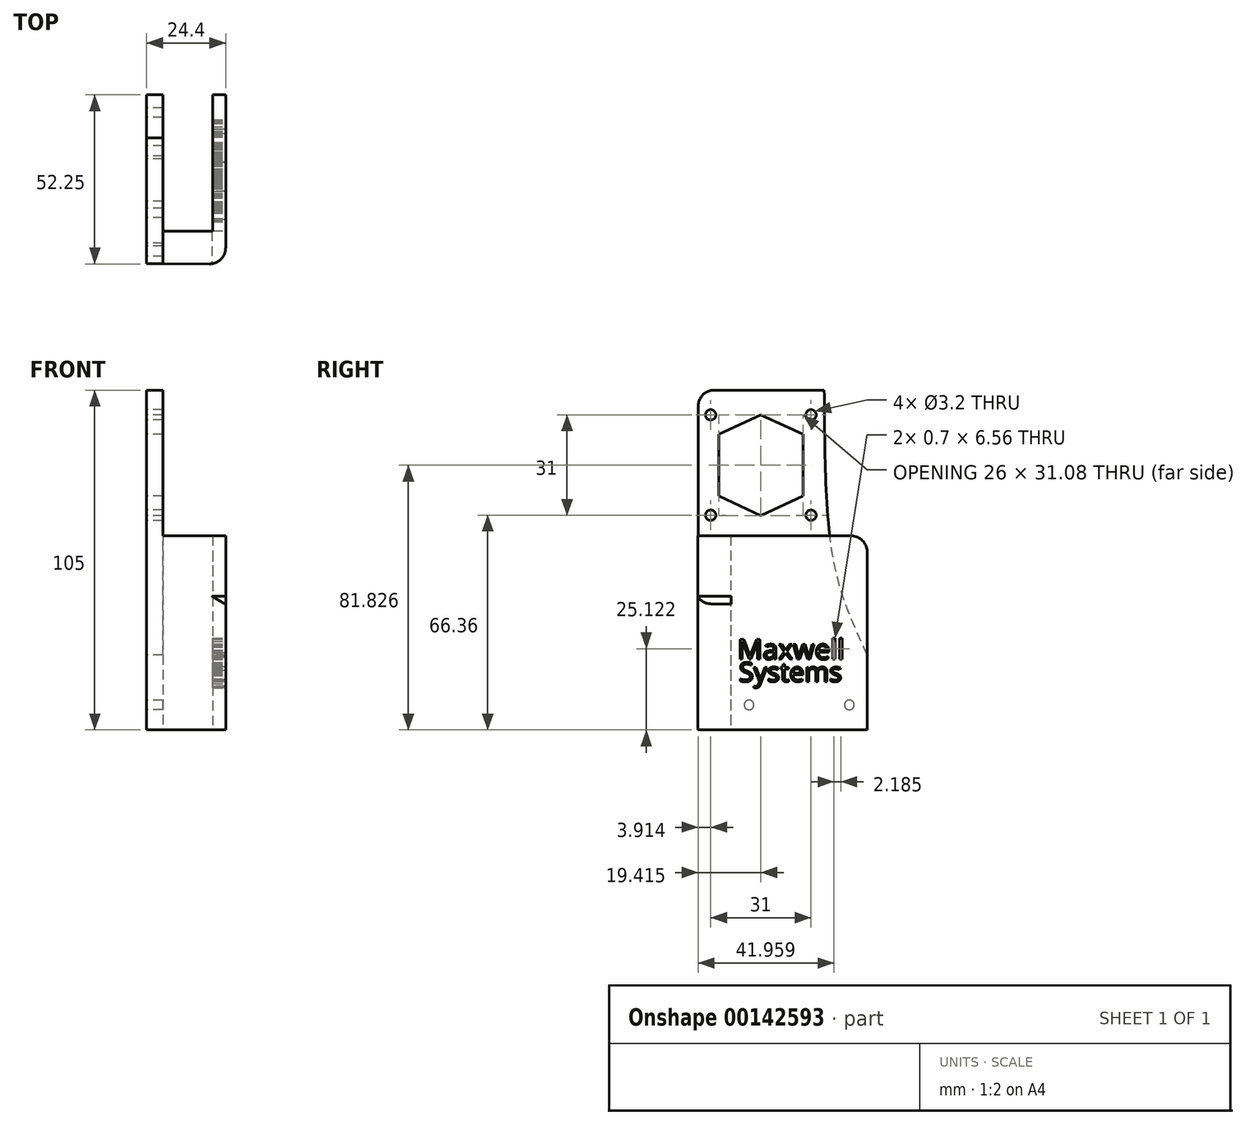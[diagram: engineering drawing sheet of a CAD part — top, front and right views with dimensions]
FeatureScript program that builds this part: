
annotation { "Feature Type Name" : "Feature", "Feature Type Description" : "" }
export const myFeature = defineFeature(function(context is Context, id is Id, definition is map)
    precondition{}
    {
        {
            var Q0;
            Q0=qCreatedBy(makeId("Top.planeOp"),FACE);
            var sketch = newSketch(context, id + "F0", { "sketchPlane" : qUnion([Q0])});
            skLineSegment(sketch, "E0.bottom", {"start": v(0, 0) * mm, "end": v(-15, 0) * mm});
            skLineSegment(sketch, "E0.top", {"start": v(0, 42) * mm, "end": v(-15, 42) * mm});
            skLineSegment(sketch, "E0.left", {"start": v(0, 0) * mm, "end": v(0, 42) * mm});
            skLineSegment(sketch, "E0.right", {"start": v(-15, 0) * mm, "end": v(-15, 42) * mm});
            skLineSegment(sketch, "E1.0", {"start": v(-15.2, -0.02) * mm, "end": v(-15.2, 42) * mm});
            skLineSegment(sketch, "E2.bottom", {"start": v(-15.2, 42) * mm, "end": v(-20.2, 42) * mm});
            skLineSegment(sketch, "E2.left", {"start": v(-15.2, 42) * mm, "end": v(-15.2, 0) * mm});
            skLineSegment(sketch, "E2.right", {"start": v(-20.2, 42) * mm, "end": v(-20.2, 0) * mm});
            skPoint(sketch, "E3.right.end.orphan", {"position": v(-20.2, -5.2) * mm});
            skLineSegment(sketch, "E4", {"start": v(-20.2, 0) * mm, "end": v(-20.2, -10.2) * mm});
            skLineSegment(sketch, "E5", {"start": v(-15.2, -0.02) * mm, "end": v(-15.2, -0.2) * mm});
            skLineSegment(sketch, "E6", {"start": v(-20.2, -10.2) * mm, "end": v(-15.2, -10.22) * mm});
            skLineSegment(sketch, "E7.0", {"start": v(0, -0.2) * mm, "end": v(-15, -0.2) * mm});
            skLineSegment(sketch, "E8", {"start": v(-15, -0.2) * mm, "end": v(-15.2, -0.2) * mm});
            skLineSegment(sketch, "E9.0", {"start": v(0.2, 0) * mm, "end": v(0.2, 41.89) * mm});
            skLineSegment(sketch, "E10", {"start": v(0.2, -0.2) * mm, "end": v(0, -0.2) * mm});
            skLineSegment(sketch, "E11", {"start": v(0.2, -0.2) * mm, "end": v(0.2, 0) * mm});
            skLineSegment(sketch, "E12.left", {"start": v(0.2, 41.89) * mm, "end": v(0.2, -0.2) * mm});
            skLineSegment(sketch, "E12.right", {"start": v(4.2, 41.89) * mm, "end": v(4.2, -10.27) * mm});
            skLineSegment(sketch, "E13", {"start": v(0, 42) * mm, "end": v(4.2, 42) * mm});
            skLineSegment(sketch, "E14", {"start": v(4.2, 41.89) * mm, "end": v(4.2, 42) * mm});
            skLineSegment(sketch, "E15", {"start": v(0.2, 41.89) * mm, "end": v(0.2, 42) * mm});
            skLineSegment(sketch, "E16", {"start": v(-15.2, -0.2) * mm, "end": v(-15.2, -10.22) * mm});
            skLineSegment(sketch, "E17", {"start": v(-15.2, -10.22) * mm, "end": v(4.2, -10.27) * mm});
            skSolve(sketch);
        }
        {
            var Q0;
            Q0=makeQuery(id+"F0.imprint","IMPRINT",FACE,{"disambiguationData":[TD([[makeQuery(id+"F0.imprint","IMPRINT",EDGE,{"derivedFrom":sQuery(id+"F0.wireOp",EDGE,"E2.bottom")}),1.0]])]});
            extrude(context, id + "F1", {"entities" : qUnion([Q0]), "depth" : 105 * mm});
        }
        {
            var Q0;
            Q0=makeQuery(id+"F1.opExtrude","SWEPT_FACE",FACE,{"disambiguationData":[OSD([sQuery(id+"F0.wireOp",EDGE,"E2.right"),sQuery(id+"F0.wireOp",EDGE,"E3.right"),sQuery(id+"F0.wireOp",EDGE,"qdzb2MuQ-bYxo-XKaB-Kbji-J9fmD8T30UYQ")])]});
            var sketch = newSketch(context, id + "F2", { "sketchPlane" : qUnion([Q0])});
            skCircle(sketch, "E18", {"center": v(-36.5, 7.75) * mm, "radius": 1.5 * mm});
            skCircle(sketch, "E19", {"center": v(-5.5, 7.75) * mm, "radius": 1.5 * mm});
            skLineSegment(sketch, "E20", {"start": v(-36.5, 7.75) * mm, "end": v(-42, 7.75) * mm, "construction": true});
            skLineSegment(sketch, "E21", {"start": v(-42, 7.75) * mm, "end": v(-42, 0) * mm, "construction": true});
            skLineSegment(sketch, "E22", {"start": v(-36.5, 7.75) * mm, "end": v(-5.5, 7.75) * mm, "construction": true});
            skSolve(sketch);
        }
        {
            var Q0;
            Q0=makeQuery(id+"F2.imprint","IMPRINT",FACE,{"disambiguationData":[TD([[makeQuery(id+"F2.imprint","IMPRINT",EDGE,{"derivedFrom":sQuery(id+"F2.wireOp",EDGE,"E18")}),1.0]])]});
            var Q1;
            Q1=makeQuery(id+"F2.imprint","IMPRINT",FACE,{"disambiguationData":[TD([[makeQuery(id+"F2.imprint","IMPRINT",EDGE,{"derivedFrom":sQuery(id+"F2.wireOp",EDGE,"E19")}),1.0]])]});
            extrude(context, id + "F3", {"entities" : qUnion([Q0, Q1]), "operationType" : NewBodyOperationType.REMOVE, "oppositeDirection" : true, "depth" : 26 * mm});
        }
        {
            var Q0;
            Q0=makeQuery(id+"F1.opExtrude","SWEPT_FACE",FACE,{"disambiguationData":[OSD([sQuery(id+"F0.wireOp",EDGE,"E2.right"),sQuery(id+"F0.wireOp",EDGE,"E3.right"),sQuery(id+"F0.wireOp",EDGE,"qdzb2MuQ-bYxo-XKaB-Kbji-J9fmD8T30UYQ")])]});
            var sketch = newSketch(context, id + "F4", { "sketchPlane" : qUnion([Q0])});
            skLineSegment(sketch, "E23", {"start": v(0, 0) * mm, "end": v(0, 35) * mm, "construction": true});
            skLineSegment(sketch, "E24", {"start": v(0, 35) * mm, "end": v(-9.15, 35) * mm, "construction": true});
            skLineSegment(sketch, "E25", {"start": v(-9.15, 35) * mm, "end": v(-9.15, 81.85) * mm, "construction": true});
            skCircle(sketch, "E26", {"center": v(-24.66, 66.36) * mm, "radius": 1.6 * mm});
            skCircle(sketch, "E27", {"center": v(6.34, 66.36) * mm, "radius": 1.6 * mm});
            skCircle(sketch, "E28", {"center": v(-24.66, 97.36) * mm, "radius": 1.6 * mm});
            skCircle(sketch, "E29", {"center": v(6.34, 97.36) * mm, "radius": 1.6 * mm});
            skPoint(sketch, "E30.endSnap0", {"position": v(-22.16, 81.86) * mm});
            skLineSegment(sketch, "E31.left", {"start": v(-22.16, 74.87) * mm, "end": v(-22.16, 72.36) * mm});
            skLineSegment(sketch, "E31.right", {"start": v(3.84, 74.87) * mm, "end": v(3.84, 72.36) * mm});
            skPoint(sketch, "E31.middle", {"position": v(-9.16, 81.86) * mm});
            skPoint(sketch, "E32.visualSharp", {"position": v(-22.16, 91.36) * mm});
            skPoint(sketch, "E33.visualSharp", {"position": v(3.84, 91.36) * mm});
            skPoint(sketch, "E34.visualSharp", {"position": v(3.84, 72.36) * mm});
            skPoint(sketch, "E35.visualSharp", {"position": v(-22.16, 72.36) * mm});
            skLineSegment(sketch, "E36", {"start": v(-22.16, 74.87) * mm, "end": v(-22.16, 91.36) * mm});
            skLineSegment(sketch, "E37", {"start": v(3.84, 74.87) * mm, "end": v(3.84, 91.36) * mm});
            skLineSegment(sketch, "E38", {"start": v(-22.16, 72.36) * mm, "end": v(-9.16, 66.29) * mm});
            skLineSegment(sketch, "E39", {"start": v(-9.16, 66.29) * mm, "end": v(3.84, 72.36) * mm});
            skLineSegment(sketch, "E40", {"start": v(3.84, 91.36) * mm, "end": v(-9.16, 97.37) * mm});
            skLineSegment(sketch, "E41", {"start": v(-22.16, 91.36) * mm, "end": v(-9.16, 97.37) * mm});
            skFitSpline(sketch, "E42", {"points": [v(-42, 23.14) * mm, v(-31.61, 52.4) * mm, v(-28.72, 105) * mm], "startDerivative": vector(25.72, 59.08) * mm, "endDerivative": vector(1.24, 74.4) * mm});
            skLineSegment(sketch, "E43", {"start": v(-28.72, 105) * mm, "end": v(-42, 105) * mm});
            skLineSegment(sketch, "E44", {"start": v(-42, 105) * mm, "end": v(-42, 23.14) * mm});
            skLineSegment(sketch, "E45", {"start": v(0, 35) * mm, "end": v(0, 51.1) * mm, "construction": true});
            skSolve(sketch);
        }
        {
            var Q0;
            Q0=makeQuery(id+"F4.imprint","IMPRINT",FACE,{"disambiguationData":[TD([[makeQuery(id+"F4.imprint","IMPRINT",EDGE,{"derivedFrom":sQuery(id+"F4.wireOp",EDGE,"E42")}),1.0]])]});
            var Q1;
            Q1=makeQuery(id+"F4.imprint","IMPRINT",FACE,{"disambiguationData":[TD([[makeQuery(id+"F4.imprint","IMPRINT",EDGE,{"derivedFrom":sQuery(id+"F4.wireOp",EDGE,"E28")}),1.0]])]});
            var Q2;
            Q2=makeQuery(id+"F4.imprint","IMPRINT",FACE,{"disambiguationData":[TD([[makeQuery(id+"F4.imprint","IMPRINT",EDGE,{"derivedFrom":sQuery(id+"F4.wireOp",EDGE,"E29")}),1.0]])]});
            var Q3;
            Q3=makeQuery(id+"F4.imprint","IMPRINT",FACE,{"disambiguationData":[TD([[makeQuery(id+"F4.imprint","IMPRINT",EDGE,{"derivedFrom":sQuery(id+"F4.wireOp",EDGE,"E27")}),1.0]])]});
            var Q4;
            Q4=makeQuery(id+"F4.imprint","IMPRINT",FACE,{"disambiguationData":[TD([[makeQuery(id+"F4.imprint","IMPRINT",EDGE,{"derivedFrom":sQuery(id+"F4.wireOp",EDGE,"E26")}),1.0]])]});
            var Q5;
            Q5=makeQuery(id+"F4.imprint","IMPRINT",FACE,{"disambiguationData":[TD([[makeQuery(id+"F4.imprint","IMPRINT",EDGE,{"derivedFrom":sQuery(id+"F4.wireOp",EDGE,"E31.left")}),1.0]])]});
            var Q6;
            Q6=makeQuery(id+"F4.imprint","IMPRINT",FACE,{"disambiguationData":[TD([[makeQuery(id+"F4.imprint","IMPRINT",EDGE,{"derivedFrom":sQuery(id+"F4.wireOp",EDGE,"r2B8Uupm-pH7r-utd8-dma5-mInYl2hJIS5c")}),1.0]])]});
            var Q7;
            Q7=makeQuery(id+"F4.imprint","IMPRINT",FACE,{"disambiguationData":[TD([[makeQuery(id+"F4.imprint","IMPRINT",EDGE,{"derivedFrom":sQuery(id+"F4.wireOp",EDGE,"BXJIOBOm-Etzu-Nobf-zrYE-yjRHMHe8ajhu")}),1.0]])]});
            extrude(context, id + "F5", {"entities" : qUnion([Q0, Q1, Q2, Q3, Q4, Q5, Q6, Q7]), "operationType" : NewBodyOperationType.REMOVE, "oppositeDirection" : true, "depth" : 25 * mm});
        }
        {
            var Q0;
            Q0=makeQuery(id+"F5.boolean.opBoolean","COPY",EDGE,{"derivedFrom":makeQuery(id+"F5.opExtrude","SWEPT_EDGE",EDGE,{"disambiguationData":[OSD([sQuery(id+"F0.wireOp",EDGE,"E2.right"),sQuery(id+"F0.wireOp",EDGE,"E4"),sQuery(id+"F4.wireOp",EDGE,"E42"),sQuery(id+"F4.wireOp",EDGE,"E43")])]})});
            var Q1;
            Q1=makeQuery(id+"F1.opExtrude","CAP_EDGE",EDGE,{"disambiguationData":[OSD([sQuery(id+"F0.wireOp",EDGE,"E6")])],"isStart":false});
            var Q2;
            Q2=makeQuery(id+"F5.boolean.opBoolean","COPY",EDGE,{"derivedFrom":makeQuery(id+"F5.opExtrude","SWEPT_EDGE",EDGE,{"disambiguationData":[OSD([sQuery(id+"F0.wireOp",EDGE,"E2.bottom"),sQuery(id+"F0.wireOp",EDGE,"E2.right"),sQuery(id+"F4.wireOp",EDGE,"E42"),sQuery(id+"F4.wireOp",EDGE,"E44")])]})});
            fillet(context, id + "F6", {"entities" : qUnion([Q0, Q1, Q2]), "radius" : 5 * mm, "tangentPropagation" : true, "allowEdgeOverflow" : false});
        }
        {
            var Q0;
            Q0=makeQuery(id+"F0.imprint","IMPRINT",FACE,{"disambiguationData":[TD([[makeQuery(id+"F0.imprint","IMPRINT",EDGE,{"derivedFrom":sQuery(id+"F0.wireOp",EDGE,"E7.0")}),1.0]])]});
            extrude(context, id + "F7", {"entities" : qUnion([Q0]), "operationType" : NewBodyOperationType.ADD, "depth" : 60 * mm});
        }
        {
            var Q0;
            Q0=makeQuery(id+"F7.opExtrude","SWEPT_FACE",FACE,{"disambiguationData":[OSD([sQuery(id+"F0.wireOp",EDGE,"E17")])]});
            var sketch = newSketch(context, id + "F8", { "sketchPlane" : qUnion([Q0])});
            skFitSpline(sketch, "E46", {"points": [v(-15.17, 60) * mm, v(-6.52, 46.29) * mm, v(4.23, 38.93) * mm, v(4.23, 38.96) * mm, v(4.23, 39.05) * mm], "startDerivative": vector(12.03, -28.42) * mm, "endDerivative": vector(0.23, 2.5) * mm});
            skLineSegment(sketch, "E47", {"start": v(0, 60) * mm, "end": v(-15.17, 60) * mm});
            skLineSegment(sketch, "E48", {"start": v(0, 41.35) * mm, "end": v(4.23, 41.35) * mm});
            skLineSegment(sketch, "E49", {"start": v(4.23, 41.35) * mm, "end": v(4.23, 60) * mm});
            skLineSegment(sketch, "E50", {"start": v(4.23, 60) * mm, "end": v(0, 60) * mm});
            skSolve(sketch);
        }
        {
            var Q0;
            Q0=makeQuery(id+"F8.imprint","IMPRINT",FACE,{"disambiguationData":[TD([[makeQuery(id+"F8.imprint","IMPRINT",EDGE,{"derivedFrom":sQuery(id+"F8.wireOp",EDGE,"E46")}),1.0]])]});
            extrude(context, id + "F9", {"entities" : qUnion([Q0]), "operationType" : NewBodyOperationType.REMOVE, "oppositeDirection" : true, "depth" : 10.2 * mm});
        }
        {
            var Q0;
            Q0=makeQuery(id+"F7.opExtrude","CAP_EDGE",EDGE,{"disambiguationData":[OSD([sQuery(id+"F0.wireOp",EDGE,"E13")])],"isStart":false});
            var Q1;
            Q1=makeQuery(id+"F7.opExtrude","SWEPT_EDGE",EDGE,{"disambiguationData":[OSD([sQuery(id+"F0.wireOp",EDGE,"E12.right"),sQuery(id+"F0.wireOp",EDGE,"E17")])]});
            var Q2;
            Q2=makeQuery(id+"F9.boolean.opBoolean","COPY",EDGE,{"derivedFrom":makeQuery(id+"F9.opExtrude","CAP_EDGE",EDGE,{"disambiguationData":[OSD([sQuery(id+"F8.wireOp",EDGE,"E47"),sQuery(id+"F8.wireOp",EDGE,"E50")])],"isStart":false})});
            fillet(context, id + "F10", {"entities" : qUnion([Q0, Q1, Q2]), "radius" : 5 * mm, "tangentPropagation" : true, "allowEdgeOverflow" : false});
        }
        {
            var Q0;
            Q0=makeQuery(id+"F7.opExtrude","SWEPT_FACE",FACE,{"disambiguationData":[OSD([sQuery(id+"F0.wireOp",EDGE,"E12.right"),sQuery(id+"F0.wireOp",EDGE,"E14")])]});
            var sketch = newSketch(context, id + "F11", { "sketchPlane" : qUnion([Q0])});
            skText(sketch, "E51", { "text": "Maxwell", "fontName": "OpenSans-Regular.ttf"});
            skText(sketch, "E52", { "text": "Systems", "fontName": "OpenSans-Regular.ttf"});
            skLineSegment(sketch, "E53", {"start": v(-5.25, 41.35) * mm, "end": v(42, 41.35) * mm, "construction": true});
            const initialGuessF11  = {"E51": [0.00192, 0.02184, 1, 0, 0.00622], "E52": [0.00238, 0.01496, 1, 0, 0.00595]};
            skSetInitialGuess(sketch, initialGuessF11);
            skSolve(sketch);
        }
        {
            var Q0;
            Q0 = qSketchRegion(id + "F11", true);
            extrude(context, id + "F12", {"entities" : qUnion([Q0]), "operationType" : NewBodyOperationType.REMOVE, "oppositeDirection" : true, "depth" : 4 * mm});
        }
    });
